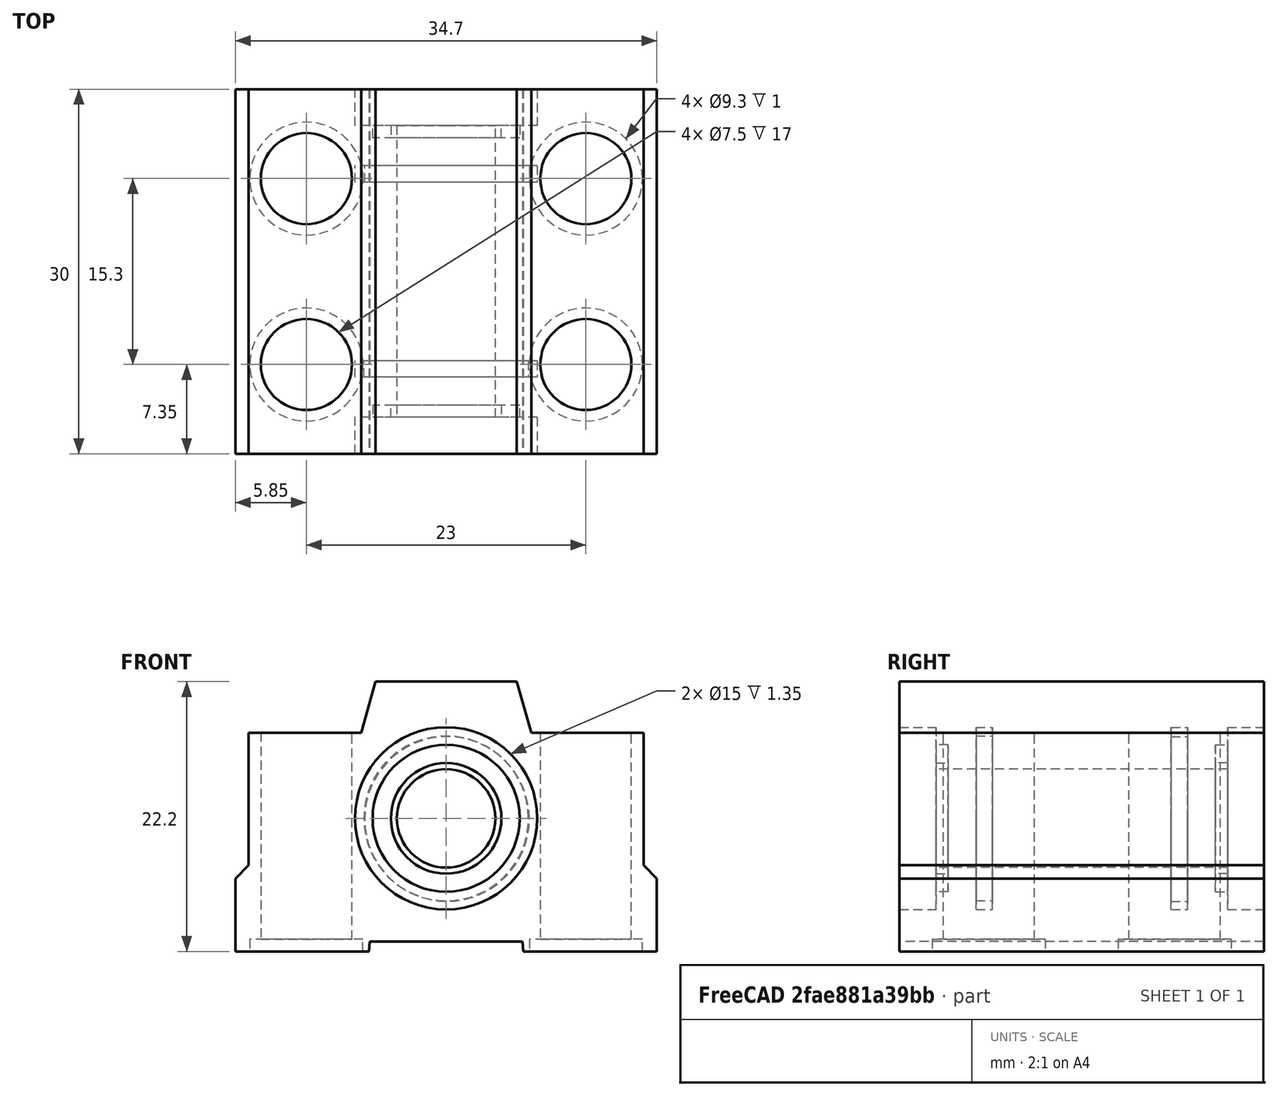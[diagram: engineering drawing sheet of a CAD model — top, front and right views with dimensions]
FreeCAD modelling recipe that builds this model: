
FCSTD DOCUMENT  (FreeCAD 0.15R4671 (Git))
Label: 8mm linear bearing with pillow block
License: CC-BY 3.0
LicenseURL: http://creativecommons.org/licenses/by/3.0/
objects: Part::Feature×2, App::MeasureDistance×2, Part::Fuse×1
note: 3 computed .brp shape members not serialized (recipe doc carries the construction recipe); baked Part::Feature solids carry a one-line shape summary decoded from their .brp

FEATURE [Part::Feature] Part__Feature  label="pillow block"
  shape: bbox 34.7 x 30 x 22.2 mm, 31 faces (baked)
FEATURE [Part::Feature] Part__Feature001  label="8mm bearing"
  Placement = pos=(0,-3,0) rot=(1,0,0;1.5708rad)
  shape: bbox 15 x 24 x 15 mm, 20 faces (baked)
FEATURE [Part::Fuse] Fusion  label="8mm linear bearing with pillow block"
  Base = -> Part__Feature
  Tool = -> Part__Feature001
FEATURE [App::MeasureDistance] Distance  label="Distance: 32.500"
  Distance = 32.5
  P1 = (16.25,0,7.05)
  P2 = (-16.25,0,7.05)
FEATURE [App::MeasureDistance] Distance001  label="Distance: 34.700"
  Distance = 34.7
  P1 = (17.35,0,-10.95)
  P2 = (-17.35,0,-10.95)
